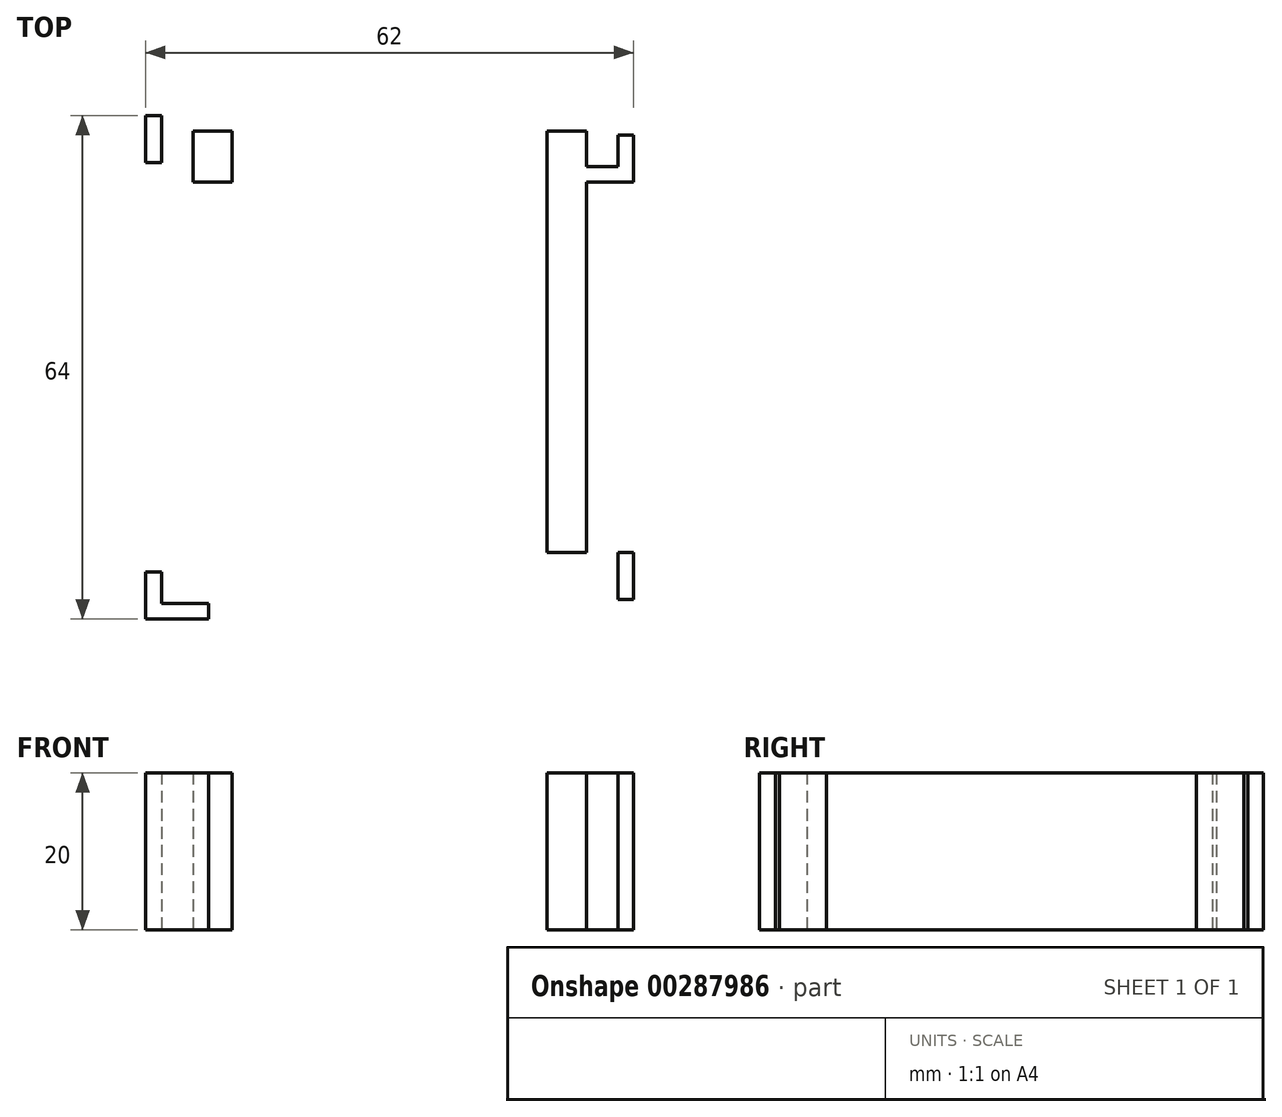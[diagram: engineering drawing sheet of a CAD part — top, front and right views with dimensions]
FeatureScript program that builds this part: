
annotation { "Feature Type Name" : "Feature", "Feature Type Description" : "" }
export const myFeature = defineFeature(function(context is Context, id is Id, definition is map)
    precondition{}
    {
        {
            var Q0;
            Q0=qCreatedBy(makeId("Top.planeOp"),FACE);
            var sketch = newSketch(context, id + "F0", { "sketchPlane" : qUnion([Q0])});
            skLineSegment(sketch, "E0.bottom", {"start": v(-25, 30) * mm, "end": v(25, 30) * mm});
            skLineSegment(sketch, "E0.top", {"start": v(-25, -30) * mm, "end": v(25, -30) * mm});
            skLineSegment(sketch, "E0.left", {"start": v(-25, 30) * mm, "end": v(-25, -30) * mm});
            skLineSegment(sketch, "E0.right", {"start": v(25, 30) * mm, "end": v(25, -30) * mm});
            skPoint(sketch, "E0.middle", {"position": v(0, 0) * mm});
            skPoint(sketch, "E1", {"position": v(25, 25.5) * mm});
            skLineSegment(sketch, "E2.bottom", {"start": v(25, 25.5) * mm, "end": v(29, 25.5) * mm});
            skLineSegment(sketch, "E2.top", {"start": v(25, 23.5) * mm, "end": v(29, 23.5) * mm});
            skLineSegment(sketch, "E2.left", {"start": v(25, 25.5) * mm, "end": v(25, 23.5) * mm});
            skLineSegment(sketch, "E2.right", {"start": v(29, 25.5) * mm, "end": v(29, 23.5) * mm});
            skLineSegment(sketch, "E3.MirrorCS", {"start": v(-25, -30) * mm, "end": v(-25, 30) * mm});
            skLineSegment(sketch, "E4.MirrorCS", {"start": v(25, -30) * mm, "end": v(25, 30) * mm});
            skLineSegment(sketch, "E5.bottom", {"start": v(-25, 23.5) * mm, "end": v(25, 23.5) * mm});
            skLineSegment(sketch, "E5.top", {"start": v(-25, -23.5) * mm, "end": v(25, -23.5) * mm});
            skLineSegment(sketch, "E5.left", {"start": v(-25, 23.5) * mm, "end": v(-25, -23.5) * mm});
            skLineSegment(sketch, "E5.right", {"start": v(25, 23.5) * mm, "end": v(25, -23.5) * mm});
            skLineSegment(sketch, "E6.MirrorCS", {"start": v(25, 30) * mm, "end": v(-25, 30) * mm});
            skLineSegment(sketch, "E7.MirrorCS", {"start": v(25, -30) * mm, "end": v(-25, -30) * mm});
            skLineSegment(sketch, "E8.MirrorCS", {"start": v(25, 23.5) * mm, "end": v(-25, 23.5) * mm});
            skLineSegment(sketch, "E9.MirrorCS", {"start": v(25, -23.5) * mm, "end": v(-25, -23.5) * mm});
            skLineSegment(sketch, "E10.bottom", {"start": v(29, 23.5) * mm, "end": v(31, 23.5) * mm});
            skLineSegment(sketch, "E10.top", {"start": v(29, 29.5) * mm, "end": v(31, 29.5) * mm});
            skLineSegment(sketch, "E10.left", {"start": v(29, 23.5) * mm, "end": v(29, 29.5) * mm});
            skLineSegment(sketch, "E10.right", {"start": v(31, 23.5) * mm, "end": v(31, 29.5) * mm});
            skLineSegment(sketch, "E11.MirrorCS", {"start": v(29, -25.5) * mm, "end": v(29, -23.5) * mm});
            skLineSegment(sketch, "E12.MirrorCS", {"start": v(29, -23.5) * mm, "end": v(31, -23.5) * mm});
            skLineSegment(sketch, "E13.MirrorCS", {"start": v(29, -29.5) * mm, "end": v(31, -29.5) * mm});
            skLineSegment(sketch, "E14.MirrorCS", {"start": v(25, -25.5) * mm, "end": v(25, -23.5) * mm});
            skLineSegment(sketch, "E15.MirrorCS", {"start": v(31, -23.5) * mm, "end": v(31, -29.5) * mm});
            skLineSegment(sketch, "E16.MirrorCS", {"start": v(29, -23.5) * mm, "end": v(29, -29.5) * mm});
            skPoint(sketch, "E17.MirrorP", {"position": v(25, -25.5) * mm});
            skLineSegment(sketch, "E18.MirrorCS", {"start": v(25, -23.5) * mm, "end": v(29, -23.5) * mm});
            skLineSegment(sketch, "E19.MirrorCS", {"start": v(25, -25.5) * mm, "end": v(29, -25.5) * mm});
            skPoint(sketch, "E20", {"position": v(-23, 30) * mm});
            skLineSegment(sketch, "E21.bottom", {"start": v(-23, 30) * mm, "end": v(-31, 30) * mm});
            skLineSegment(sketch, "E21.top", {"start": v(-23, 32) * mm, "end": v(-31, 32) * mm});
            skLineSegment(sketch, "E21.left", {"start": v(-23, 30) * mm, "end": v(-23, 32) * mm});
            skLineSegment(sketch, "E21.right", {"start": v(-31, 30) * mm, "end": v(-31, 32) * mm});
            skLineSegment(sketch, "E22.bottom", {"start": v(-31, 32) * mm, "end": v(-29, 32) * mm});
            skLineSegment(sketch, "E22.top", {"start": v(-31, 26) * mm, "end": v(-29, 26) * mm});
            skLineSegment(sketch, "E22.left", {"start": v(-31, 32) * mm, "end": v(-31, 26) * mm});
            skLineSegment(sketch, "E22.right", {"start": v(-29, 32) * mm, "end": v(-29, 26) * mm});
            skLineSegment(sketch, "E23.MirrorCS", {"start": v(-31, -32) * mm, "end": v(-29, -32) * mm});
            skLineSegment(sketch, "E24.MirrorCS", {"start": v(-23, -30) * mm, "end": v(-23, -32) * mm});
            skLineSegment(sketch, "E25.MirrorCS", {"start": v(-31, -30) * mm, "end": v(-31, -32) * mm});
            skLineSegment(sketch, "E26.MirrorCS", {"start": v(-23, -30) * mm, "end": v(-31, -30) * mm});
            skPoint(sketch, "E27.MirrorP", {"position": v(-23, -30) * mm});
            skLineSegment(sketch, "E28.MirrorCS", {"start": v(-23, -32) * mm, "end": v(-31, -32) * mm});
            skLineSegment(sketch, "E29.MirrorCS", {"start": v(-31, -26) * mm, "end": v(-29, -26) * mm});
            skLineSegment(sketch, "E30.MirrorCS", {"start": v(-29, -32) * mm, "end": v(-29, -26) * mm});
            skLineSegment(sketch, "E31.MirrorCS", {"start": v(-31, -32) * mm, "end": v(-31, -26) * mm});
            skLineSegment(sketch, "E32.bottom", {"start": v(-20, 30) * mm, "end": v(20, 30) * mm});
            skLineSegment(sketch, "E32.top", {"start": v(-20, -30) * mm, "end": v(20, -30) * mm});
            skLineSegment(sketch, "E32.left", {"start": v(-20, 30) * mm, "end": v(-20, -30) * mm});
            skLineSegment(sketch, "E32.right", {"start": v(20, 30) * mm, "end": v(20, -30) * mm});
            skSolve(sketch);
        }
        {
            var Q0;
            {var subQ3=sQuery(id+"F0.wireOp",EDGE,"E7.MirrorCS");Q0=makeQuery(id+"F0.imprint","IMPRINT",FACE,{"disambiguationData":[TD([[makeQuery(id+"F0.imprint","IMPRINT",EDGE,{"derivedFrom":subQ3}),-1.0]])]});}
            var Q1;
            Q1=makeQuery(id+"F0.imprint","IMPRINT",FACE,{"disambiguationData":[TD([[makeQuery(id+"F0.imprint","IMPRINT",EDGE,{"derivedFrom":sQuery(id+"F0.wireOp",EDGE,"E14.MirrorCS")}),-1.0]])]});
            var Q2;
            {var subQ1=sQuery(id+"F0.wireOp",EDGE,"E12.MirrorCS");Q2=makeQuery(id+"F0.imprint","IMPRINT",FACE,{"disambiguationData":[TD([[makeQuery(id+"F0.imprint","IMPRINT",EDGE,{"derivedFrom":subQ1}),-1.0]])]});}
            var Q3;
            {var subQ0=sQuery(id+"F0.wireOp",EDGE,"E2.bottom");Q3=makeQuery(id+"F0.imprint","IMPRINT",FACE,{"disambiguationData":[TD([[makeQuery(id+"F0.imprint","IMPRINT",EDGE,{"derivedFrom":subQ0}),-1.0]])]});}
            var Q4;
            {var subQ3=sQuery(id+"F0.wireOp",EDGE,"E10.bottom");Q4=makeQuery(id+"F0.imprint","IMPRINT",FACE,{"disambiguationData":[TD([[makeQuery(id+"F0.imprint","IMPRINT",EDGE,{"derivedFrom":subQ3}),1.0]])]});}
            var Q5;
            {var subQ1=sQuery(id+"F0.wireOp",EDGE,"E21.top");Q5=makeQuery(id+"F0.imprint","IMPRINT",FACE,{"disambiguationData":[TD([[makeQuery(id+"F0.imprint","IMPRINT",EDGE,{"derivedFrom":subQ1}),1.0]])]});}
            var Q6;
            {var subQ5=sQuery(id+"F0.wireOp",EDGE,"E22.bottom");Q6=makeQuery(id+"F0.imprint","IMPRINT",FACE,{"disambiguationData":[TD([[makeQuery(id+"F0.imprint","IMPRINT",EDGE,{"derivedFrom":subQ5}),-1.0]])]});}
            var Q7;
            {var subQ5=sQuery(id+"F0.wireOp",EDGE,"E22.top");Q7=makeQuery(id+"F0.imprint","IMPRINT",FACE,{"disambiguationData":[TD([[makeQuery(id+"F0.imprint","IMPRINT",EDGE,{"derivedFrom":subQ5}),1.0]])]});}
            var Q8;
            {var subQ2=sQuery(id+"F0.wireOp",EDGE,"E24.MirrorCS");Q8=makeQuery(id+"F0.imprint","IMPRINT",FACE,{"disambiguationData":[TD([[makeQuery(id+"F0.imprint","IMPRINT",EDGE,{"derivedFrom":subQ2}),-1.0]])]});}
            var Q9;
            {var subQ0=sQuery(id+"F0.wireOp",EDGE,"E28.MirrorCS");var subQ1=sQuery(id+"F0.wireOp",EDGE,"E30.MirrorCS");var subQ2=makeQuery(id+"F0.imprint","INTERSECT",VERTEX,{"derivedFrom":[subQ1,subQ0]});Q9=makeQuery(id+"F0.imprint","IMPRINT",FACE,{"disambiguationData":[TD([[makeQuery(id+"F0.imprint","IMPRINT",EDGE,{"disambiguationData":[TD([[subQ2,-1.0]])],"derivedFrom":subQ1}),1.0]])]});}
            var Q10;
            {var subQ0=sQuery(id+"F0.wireOp",EDGE,"E29.MirrorCS");Q10=makeQuery(id+"F0.imprint","IMPRINT",FACE,{"disambiguationData":[TD([[makeQuery(id+"F0.imprint","IMPRINT",EDGE,{"derivedFrom":subQ0}),-1.0]])]});}
            var Q11;
            {var subQ0=sQuery(id+"F0.wireOp",EDGE,"E21.bottom");var subQ5=sQuery(id+"F0.wireOp",EDGE,"E0.left");var subQ6=makeQuery(id+"F0.imprint","INTERSECT",VERTEX,{"derivedFrom":[subQ5,subQ0]});Q11=makeQuery(id+"F0.imprint","IMPRINT",FACE,{"disambiguationData":[TD([[makeQuery(id+"F0.imprint","IMPRINT",EDGE,{"disambiguationData":[TD([[subQ6,-1.0]])],"derivedFrom":subQ5}),1.0]])]});}
            var Q12;
            {var subQ0=sQuery(id+"F0.wireOp",EDGE,"E0.right");var subQ1=makeQuery(id+"F0.imprint","INTERSECT",VERTEX,{"derivedFrom":[sQuery(id+"F0.wireOp",EDGE,"E2.bottom"),subQ0]});Q12=makeQuery(id+"F0.imprint","IMPRINT",FACE,{"disambiguationData":[TD([[makeQuery(id+"F0.imprint","IMPRINT",EDGE,{"disambiguationData":[TD([[subQ1,1.0]])],"derivedFrom":subQ0}),-1.0]])]});}
            var Q13;
            {var subQ0=sQuery(id+"F0.wireOp",EDGE,"E5.left");Q13=makeQuery(id+"F0.imprint","IMPRINT",FACE,{"disambiguationData":[TD([[makeQuery(id+"F0.imprint","IMPRINT",EDGE,{"derivedFrom":subQ0}),1.0]])]});}
            var Q14;
            {var subQ1=sQuery(id+"F0.wireOp",EDGE,"E8.MirrorCS");var subQ3=sQuery(id+"F0.wireOp",EDGE,"E32.right");var subQ4=makeQuery(id+"F0.imprint","INTERSECT",VERTEX,{"derivedFrom":[subQ1,subQ3]});Q14=makeQuery(id+"F0.imprint","IMPRINT",FACE,{"disambiguationData":[TD([[makeQuery(id+"F0.imprint","IMPRINT",EDGE,{"disambiguationData":[TD([[subQ4,-1.0]])],"derivedFrom":subQ3}),1.0]])]});}
            extrude(context, id + "F1", {"entities" : qUnion([Q0, Q1, Q2, Q3, Q4, Q5, Q6, Q7, Q8, Q9, Q10, Q11, Q12, Q13, Q14]), "depth" : 20 * mm});
        }
    });
